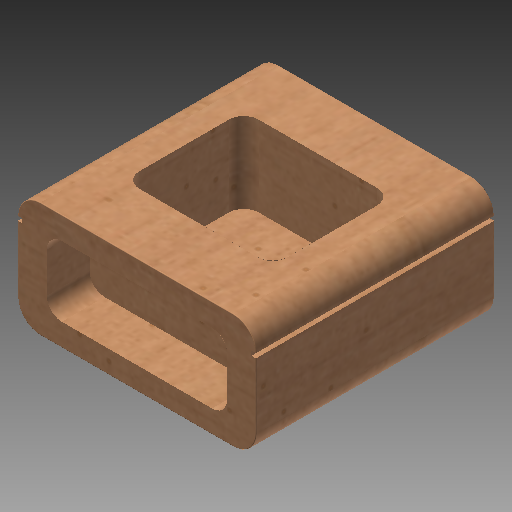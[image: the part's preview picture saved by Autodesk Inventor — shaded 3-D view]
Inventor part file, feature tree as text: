
AUTODESK INVENTOR PART (.ipt)
format: ipt  version: 2018 (Build 220112000, 112)  size: 339,968 bytes
history: native  units: in
note: dims shown in document units (in); Inventor stores cm internally (conversion verified against a paired STEP export)
features: extrude x4, sketch x4, fillet x2
ambient origin geometry x8: Origin, YZ Plane, XZ Plane, XY Plane, X Axis, Y Axis, Z Axis, Center Point
bodies: Solid1 (feature_tree)
feature tree (10):
  extrude  "Extrusion1"  Depth=1.53in
  extrude  "Extrusion2"  Depth=2.4in
  extrude  "Extrusion3"  Depth=0.57in TaperAngle=0.0deg
  extrude  "Extrusion4"  Depth=2.5in
  fillet  "Fillet1"  Radius=1.0in
  fillet  "Fillet2"  Radius=0.57in
  sketch  "Sketch1"  dims[d0=3.17in d1=1.53in]
  sketch  "Sketch2"  dims[d2=3.17in d3=0.0in d4=2.4in]
  sketch  "Sketch3"  dims[d5=0.93in d7=0.57in d8=0.0in]
  sketch  "Sketch4"  dims[d9=0.2in d10=2.5in d11=1.0in d12=0.57in d13=0.0in d14=0.3in d15=0.82in d16=1.59in d17=1.975in d18=1.07in d19=0.0in d20=0.06in d21=0.3in d23=0.01in]
